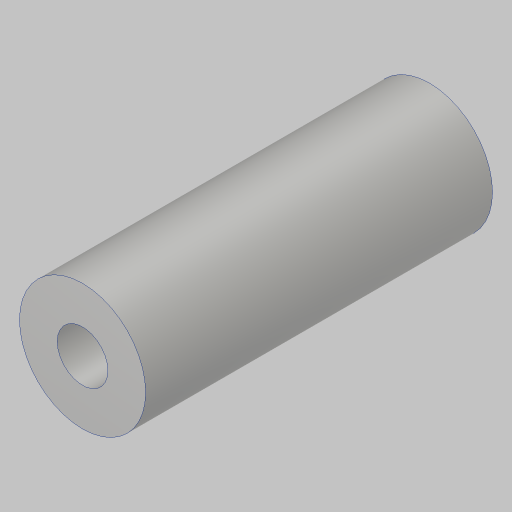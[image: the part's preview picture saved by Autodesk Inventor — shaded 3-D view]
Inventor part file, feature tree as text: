
AUTODESK INVENTOR PART (.ipt)
format: ipt  version: 2023.5 (Build 275446000, 446)  size: 111,616 bytes
history: native  units: in
note: dims shown in document units (in); Inventor stores cm internally (conversion verified against a paired STEP export)
features: extrude x1, hole x1
ambient origin geometry x8: Origin, YZ Plane, XZ Plane, XY Plane, X Axis, Y Axis, Z Axis, Center Point
bodies: Solid1 (feature_tree)
feature tree (2):
  extrude  "Extrusion1"  Depth=1.375in
  hole  "Hole1"  [1 undecoded]
note: 1 required parameter value undecoded (feature->parameter linkage not recoverable at this tier; creation-order binding heuristic only, values carry confidence <= 0.55)
